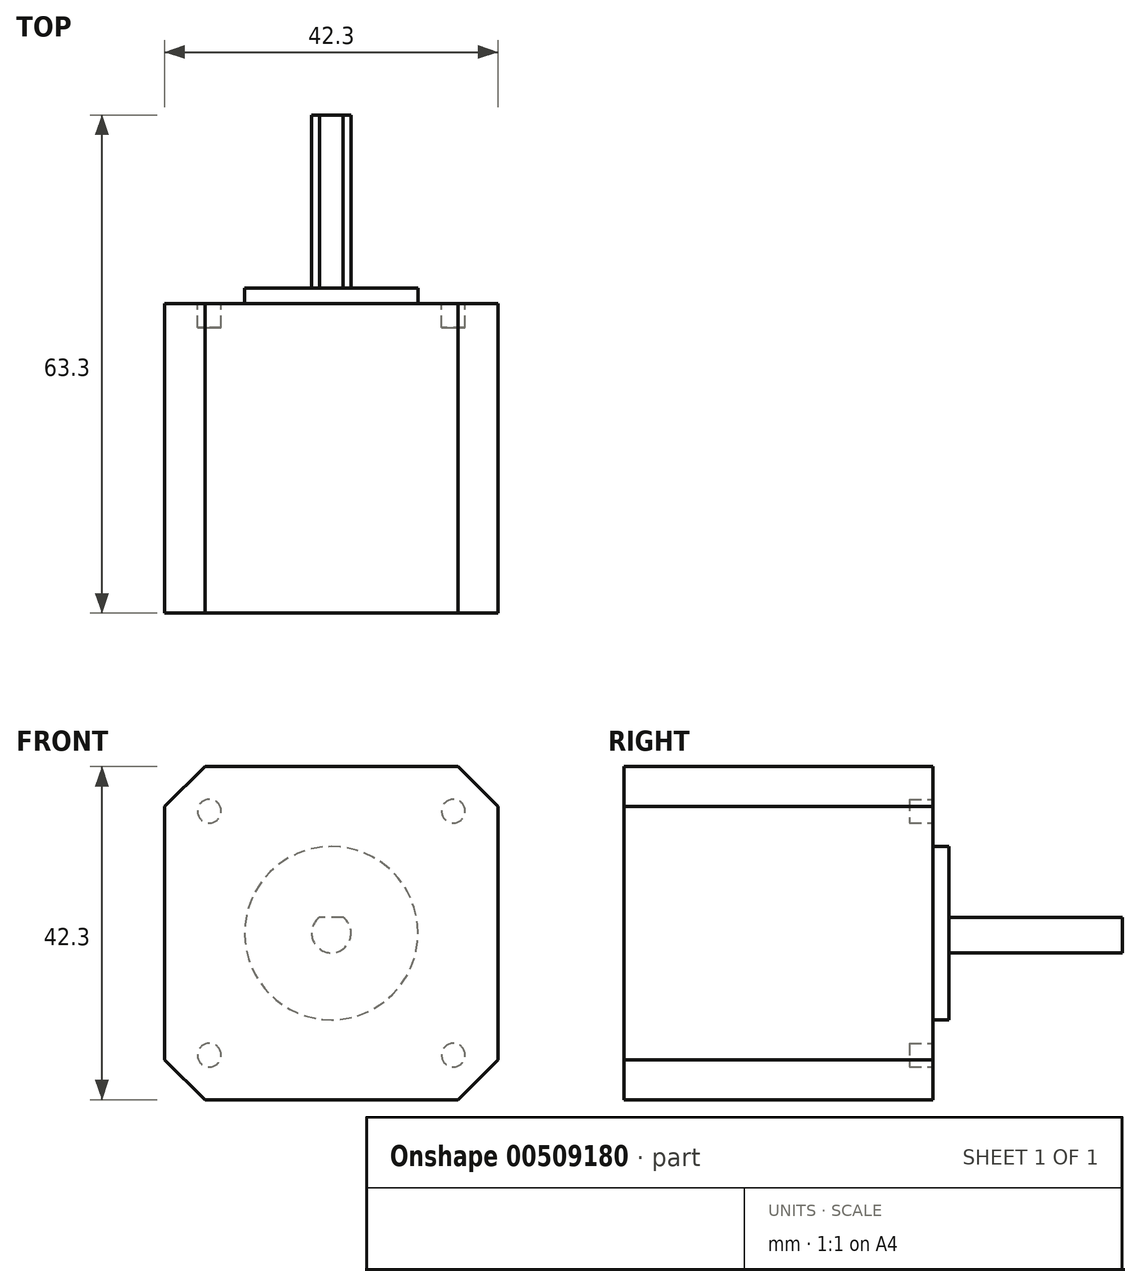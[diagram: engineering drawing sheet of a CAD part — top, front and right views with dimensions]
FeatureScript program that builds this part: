
annotation { "Feature Type Name" : "Feature", "Feature Type Description" : "" }
export const myFeature = defineFeature(function(context is Context, id is Id, definition is map)
    precondition{}
    {
        {
            var Q0;
            Q0=qCreatedBy(makeId("Front.planeOp"),FACE);
            var sketch = newSketch(context, id + "F0", { "sketchPlane" : qUnion([Q0])});
            skLineSegment(sketch, "E0.bottom", {"start": v(-21.15, 21.15) * mm, "end": v(21.15, 21.15) * mm});
            skLineSegment(sketch, "E0.top", {"start": v(-21.15, -21.15) * mm, "end": v(21.15, -21.15) * mm});
            skLineSegment(sketch, "E0.left", {"start": v(-21.15, 21.15) * mm, "end": v(-21.15, -21.15) * mm});
            skLineSegment(sketch, "E0.right", {"start": v(21.15, 21.15) * mm, "end": v(21.15, -21.15) * mm});
            skPoint(sketch, "E1", {"position": v(0, 21.15) * mm});
            skPoint(sketch, "E2", {"position": v(-21.15, 0) * mm});
            skSolve(sketch);
        }
        {
            var Q0;
            Q0=makeQuery(id+"F0.imprint","IMPRINT",FACE,{"disambiguationData":[TD([[makeQuery(id+"F0.imprint","IMPRINT",EDGE,{"derivedFrom":sQuery(id+"F0.wireOp",EDGE,"E0.bottom")}),-1.0]])]});
            extrude(context, id + "F1", {"entities" : qUnion([Q0]), "depth" : 39.3 * mm});
        }
        {
            var Q0;
            Q0=makeQuery(id+"F1.opExtrude","SWEPT_EDGE",EDGE,{"disambiguationData":[OSD([sQuery(id+"F0.wireOp",EDGE,"E0.bottom"),sQuery(id+"F0.wireOp",EDGE,"E0.left")])]});
            var Q1;
            Q1=makeQuery(id+"F1.opExtrude","SWEPT_EDGE",EDGE,{"disambiguationData":[OSD([sQuery(id+"F0.wireOp",EDGE,"E0.bottom"),sQuery(id+"F0.wireOp",EDGE,"E0.right")])]});
            var Q2;
            Q2=makeQuery(id+"F1.opExtrude","SWEPT_EDGE",EDGE,{"disambiguationData":[OSD([sQuery(id+"F0.wireOp",EDGE,"E0.top"),sQuery(id+"F0.wireOp",EDGE,"E0.right")])]});
            var Q3;
            Q3=makeQuery(id+"F1.opExtrude","SWEPT_EDGE",EDGE,{"disambiguationData":[OSD([sQuery(id+"F0.wireOp",EDGE,"E0.top"),sQuery(id+"F0.wireOp",EDGE,"E0.left")])]});
            chamfer(context, id + "F2", {"entities" : qUnion([Q0, Q1, Q2, Q3]), "width" : 5.08 * mm, "tangentPropagation" : true});
        }
        {
            var Q0;
            Q0=makeQuery(id+"F1.opExtrude","CAP_FACE",FACE,{"disambiguationData":[OSD([sQuery(id+"F0.wireOp",EDGE,"E0.bottom"),sQuery(id+"F0.wireOp",EDGE,"E0.top"),sQuery(id+"F0.wireOp",EDGE,"E0.left"),sQuery(id+"F0.wireOp",EDGE,"E0.right")])],"isStart":true});
            var sketch = newSketch(context, id + "F3", { "sketchPlane" : qUnion([Q0])});
            skLineSegment(sketch, "E3", {"start": v(-15.5, 21.15) * mm, "end": v(-15.5, -21.15) * mm, "construction": true});
            skLineSegment(sketch, "E4", {"start": v(15.5, 21.15) * mm, "end": v(15.5, -21.15) * mm, "construction": true});
            skLineSegment(sketch, "E5", {"start": v(-15.5, 15.5) * mm, "end": v(15.5, 15.5) * mm, "construction": true});
            skPoint(sketch, "E6", {"position": v(0, 15.5) * mm});
            skLineSegment(sketch, "E7", {"start": v(-15.5, -15.5) * mm, "end": v(15.5, -15.5) * mm, "construction": true});
            skLineSegment(sketch, "E8", {"start": v(15.5, 15.5) * mm, "end": v(15.5, -15.5) * mm, "construction": true});
            skPoint(sketch, "E9", {"position": v(15.5, 0) * mm});
            skCircle(sketch, "E10", {"center": v(-15.5, 15.5) * mm, "radius": 1.5 * mm});
            skCircle(sketch, "E11.MirrorC", {"center": v(15.5, 15.5) * mm, "radius": 1.5 * mm});
            skCircle(sketch, "E12.MirrorC", {"center": v(15.5, -15.5) * mm, "radius": 1.5 * mm});
            skCircle(sketch, "E13.MirrorC", {"center": v(-15.5, -15.5) * mm, "radius": 1.5 * mm});
            skSolve(sketch);
        }
        {
            var Q0;
            Q0 = qSketchRegion(id + "F3", true);
            extrude(context, id + "F4", {"entities" : qUnion([Q0]), "operationType" : NewBodyOperationType.REMOVE, "oppositeDirection" : true, "depth" : 3 * mm});
        }
        {
            var Q0;
            Q0=makeQuery(id+"F1.opExtrude","CAP_FACE",FACE,{"disambiguationData":[OSD([sQuery(id+"F0.wireOp",EDGE,"E0.bottom"),sQuery(id+"F0.wireOp",EDGE,"E0.top"),sQuery(id+"F0.wireOp",EDGE,"E0.left"),sQuery(id+"F0.wireOp",EDGE,"E0.right")])],"isStart":true});
            var sketch = newSketch(context, id + "F5", { "sketchPlane" : qUnion([Q0])});
            skCircle(sketch, "E14", {"center": v(0, 0) * mm, "radius": 11 * mm});
            skSolve(sketch);
        }
        {
            var Q0;
            Q0=makeQuery(id+"F5.imprint","IMPRINT",FACE,{"disambiguationData":[TD([[makeQuery(id+"F5.imprint","IMPRINT",EDGE,{"derivedFrom":sQuery(id+"F5.wireOp",EDGE,"E14")}),1.0]])]});
            extrude(context, id + "F6", {"entities" : qUnion([Q0]), "operationType" : NewBodyOperationType.ADD, "depth" : 2 * mm});
        }
        {
            var Q0;
            Q0=makeQuery(id+"F6.opExtrude","CAP_FACE",FACE,{"disambiguationData":[OSD([sQuery(id+"F5.wireOp",EDGE,"E14")])],"isStart":false});
            var sketch = newSketch(context, id + "F7", { "sketchPlane" : qUnion([Q0])});
            skArc(sketch, "E15", {"start": v(-1.5, 2) * mm, "mid": v(0, -2.5) * mm, "end": v(1.5, 2) * mm});
            skLineSegment(sketch, "E16", {"start": v(-1.5, 2) * mm, "end": v(1.5, 2) * mm});
            skSolve(sketch);
        }
        {
            var Q0;
            Q0 = qSketchRegion(id + "F7", true);
            extrude(context, id + "F8", {"entities" : qUnion([Q0]), "operationType" : NewBodyOperationType.ADD, "depth" : 22 * mm});
        }
    });
